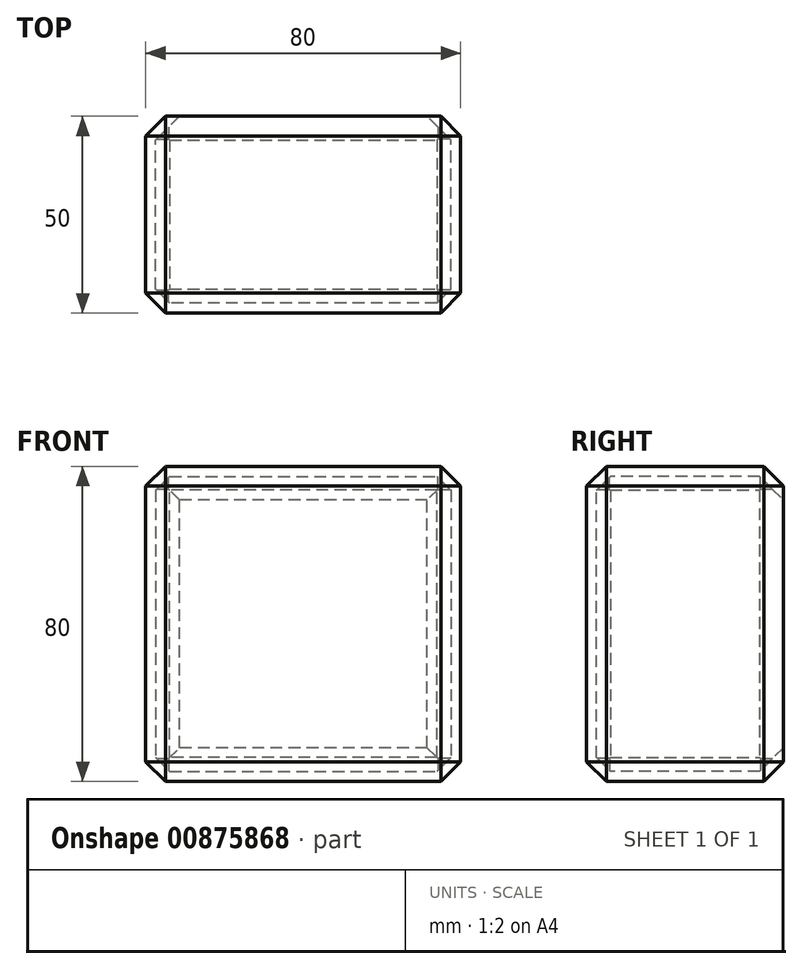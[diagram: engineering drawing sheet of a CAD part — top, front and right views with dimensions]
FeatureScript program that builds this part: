
annotation { "Feature Type Name" : "Feature", "Feature Type Description" : "" }
export const myFeature = defineFeature(function(context is Context, id is Id, definition is map)
    precondition{}
    {
        {
            var Q0;
            Q0=qCreatedBy(makeId("Top.planeOp"),FACE);
            var sketch = newSketch(context, id + "F0", { "sketchPlane" : qUnion([Q0])});
            skLineSegment(sketch, "E0.bottom", {"start": v(-48.4, 24.96) * mm, "end": v(31.6, 24.96) * mm});
            skLineSegment(sketch, "E0.top", {"start": v(-48.4, -25.04) * mm, "end": v(31.6, -25.04) * mm});
            skLineSegment(sketch, "E0.left", {"start": v(-48.4, 24.96) * mm, "end": v(-48.4, -25.04) * mm});
            skLineSegment(sketch, "E0.right", {"start": v(31.6, 24.96) * mm, "end": v(31.6, -25.04) * mm});
            skSolve(sketch);
        }
        {
            var Q0;
            Q0=makeQuery(id+"F0.imprint","IMPRINT",FACE,{"disambiguationData":[TD([[makeQuery(id+"F0.imprint","IMPRINT",EDGE,{"derivedFrom":sQuery(id+"F0.wireOp",EDGE,"E0.bottom")}),-1.0]])]});
            extrude(context, id + "F1", {"entities" : qUnion([Q0]), "depth" : 80 * mm, "offsetDistance" : 25 * mm});
        }
        {
            var Q0;
            Q0=makeQuery(id+"F1.opExtrude","CAP_EDGE",EDGE,{"disambiguationData":[OSD([sQuery(id+"F0.wireOp",EDGE,"E0.right")])],"isStart":false});
            var Q1;
            Q1=makeQuery(id+"F1.opExtrude","SWEPT_EDGE",EDGE,{"disambiguationData":[OSD([sQuery(id+"F0.wireOp",EDGE,"E0.top"),sQuery(id+"F0.wireOp",EDGE,"E0.right")])]});
            var Q2;
            Q2=makeQuery(id+"F1.opExtrude","CAP_EDGE",EDGE,{"disambiguationData":[OSD([sQuery(id+"F0.wireOp",EDGE,"E0.right")])],"isStart":true});
            var Q3;
            Q3=makeQuery(id+"F1.opExtrude","SWEPT_EDGE",EDGE,{"disambiguationData":[OSD([sQuery(id+"F0.wireOp",EDGE,"E0.bottom"),sQuery(id+"F0.wireOp",EDGE,"E0.right")])]});
            var Q4;
            Q4=makeQuery(id+"F1.opExtrude","CAP_EDGE",EDGE,{"disambiguationData":[OSD([sQuery(id+"F0.wireOp",EDGE,"E0.left")])],"isStart":false});
            var Q5;
            Q5=makeQuery(id+"F1.opExtrude","SWEPT_FACE",FACE,{"disambiguationData":[OSD([sQuery(id+"F0.wireOp",EDGE,"E0.bottom")])]});
            var Q6;
            Q6=makeQuery(id+"F1.opExtrude","CAP_FACE",FACE,{"disambiguationData":[OSD([sQuery(id+"F0.wireOp",EDGE,"E0.bottom"),sQuery(id+"F0.wireOp",EDGE,"E0.top"),sQuery(id+"F0.wireOp",EDGE,"E0.left"),sQuery(id+"F0.wireOp",EDGE,"E0.right")])],"isStart":false});
            var Q7;
            Q7=makeQuery(id+"F1.opExtrude","CAP_FACE",FACE,{"disambiguationData":[OSD([sQuery(id+"F0.wireOp",EDGE,"E0.bottom"),sQuery(id+"F0.wireOp",EDGE,"E0.top"),sQuery(id+"F0.wireOp",EDGE,"E0.left"),sQuery(id+"F0.wireOp",EDGE,"E0.right")])],"isStart":true});
            var Q8;
            Q8=makeQuery(id+"F1.opExtrude","SWEPT_FACE",FACE,{"disambiguationData":[OSD([sQuery(id+"F0.wireOp",EDGE,"E0.left")])]});
            chamfer(context, id + "F2", {"entities" : qUnion([Q0, Q1, Q2, Q3, Q4, Q5, Q6, Q7, Q8]), "width" : 5 * mm, "tangentPropagation" : true});
        }
        {
            var Q0;
            Q0=makeQuery(id+"F1.opExtrude","SWEPT_FACE",FACE,{"disambiguationData":[OSD([sQuery(id+"F0.wireOp",EDGE,"E0.bottom")])]});
            shell(context, id + "F3", {"entities" : qUnion([Q0]), "thickness" : 2.5 * mm});
        }
    });
